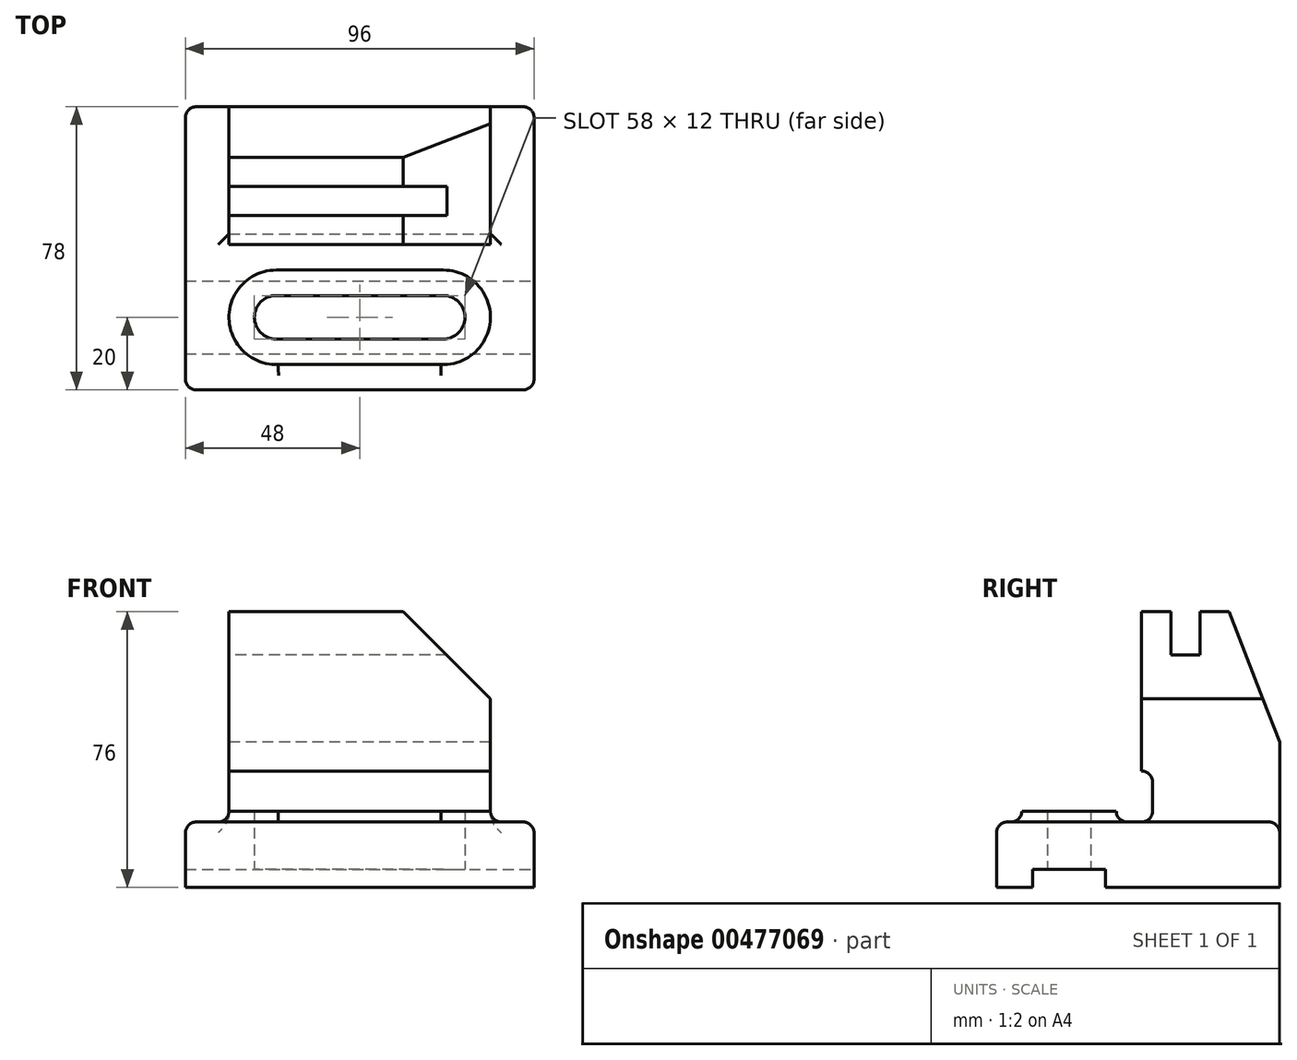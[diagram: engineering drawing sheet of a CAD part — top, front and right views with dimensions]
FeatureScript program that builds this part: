
annotation { "Feature Type Name" : "Feature", "Feature Type Description" : "" }
export const myFeature = defineFeature(function(context is Context, id is Id, definition is map)
    precondition{}
    {
        {
            var Q0;
            Q0=qCreatedBy(makeId("Top.planeOp"),FACE);
            var sketch = newSketch(context, id + "F0", { "sketchPlane" : qUnion([Q0])});
            skLineSegment(sketch, "E0.bottom", {"start": v(0, 0) * mm, "end": v(96, 0) * mm});
            skLineSegment(sketch, "E0.top", {"start": v(0, 78) * mm, "end": v(96, 78) * mm});
            skLineSegment(sketch, "E0.left", {"start": v(0, 0) * mm, "end": v(0, 78) * mm});
            skLineSegment(sketch, "E0.right", {"start": v(96, 0) * mm, "end": v(96, 78) * mm});
            skSolve(sketch);
        }
        {
            var Q0;
            Q0 = qSketchRegion(id + "F0", true);
            extrude(context, id + "F1", {"entities" : qUnion([Q0]), "depth" : 18 * mm});
        }
        {
            var Q0;
            Q0=makeQuery(id+"F1.opExtrude","CAP_FACE",FACE,{"disambiguationData":[OSD([sQuery(id+"F0.wireOp",EDGE,"E0.bottom"),sQuery(id+"F0.wireOp",EDGE,"E0.top"),sQuery(id+"F0.wireOp",EDGE,"E0.left"),sQuery(id+"F0.wireOp",EDGE,"E0.right")])],"isStart":false});
            var sketch = newSketch(context, id + "F2", { "sketchPlane" : qUnion([Q0])});
            skLineSegment(sketch, "E1.bottom", {"start": v(12, 78) * mm, "end": v(84, 78) * mm});
            skLineSegment(sketch, "E1.top", {"start": v(12, 40) * mm, "end": v(84, 40) * mm});
            skLineSegment(sketch, "E1.left", {"start": v(12, 78) * mm, "end": v(12, 40) * mm});
            skLineSegment(sketch, "E1.right", {"start": v(84, 78) * mm, "end": v(84, 40) * mm});
            skSolve(sketch);
        }
        {
            var Q0;
            Q0 = qSketchRegion(id + "F2", true);
            extrude(context, id + "F3", {"entities" : qUnion([Q0]), "operationType" : NewBodyOperationType.ADD, "depth" : 58 * mm});
        }
        {
            var Q0;
            Q0=makeQuery(id+"F1.opExtrude","SWEPT_FACE",FACE,{"disambiguationData":[OSD([sQuery(id+"F0.wireOp",EDGE,"E0.right")])]});
            var sketch = newSketch(context, id + "F4", { "sketchPlane" : qUnion([Q0])});
            skLineSegment(sketch, "E2.bottom", {"start": v(10, 0) * mm, "end": v(30, 0) * mm});
            skLineSegment(sketch, "E2.top", {"start": v(10, 5) * mm, "end": v(30, 5) * mm});
            skLineSegment(sketch, "E2.left", {"start": v(10, 0) * mm, "end": v(10, 5) * mm});
            skLineSegment(sketch, "E2.right", {"start": v(30, 0) * mm, "end": v(30, 5) * mm});
            skSolve(sketch);
        }
        {
            var Q0;
            Q0 = qSketchRegion(id + "F4", true);
            extrude(context, id + "F5", {"entities" : qUnion([Q0]), "operationType" : NewBodyOperationType.REMOVE, "endBound" : BoundingType.THROUGH_ALL, "oppositeDirection" : true, "depth" : 25 * mm});
        }
        {
            var Q0;
            Q0=makeQuery(id+"F3.opExtrude","SWEPT_FACE",FACE,{"disambiguationData":[OSD([sQuery(id+"F2.wireOp",EDGE,"E1.top")])]});
            var sketch = newSketch(context, id + "F6", { "sketchPlane" : qUnion([Q0])});
            skLineSegment(sketch, "E3.bottom", {"start": v(84, 76) * mm, "end": v(60, 76) * mm});
            skLineSegment(sketch, "E3.top", {"start": v(84, 52) * mm, "end": v(60, 52) * mm});
            skLineSegment(sketch, "E3.left", {"start": v(84, 76) * mm, "end": v(84, 52) * mm});
            skLineSegment(sketch, "E3.right", {"start": v(60, 76) * mm, "end": v(60, 52) * mm});
            skLineSegment(sketch, "E4", {"start": v(60, 76) * mm, "end": v(84, 52) * mm});
            skSolve(sketch);
        }
        {
            var Q0;
            Q0=makeQuery(id+"F6.imprint","IMPRINT",FACE,{"disambiguationData":[TD([[makeQuery(id+"F6.imprint","IMPRINT",EDGE,{"derivedFrom":sQuery(id+"F6.wireOp",EDGE,"E3.bottom")}),-1.0]])]});
            extrude(context, id + "F7", {"entities" : qUnion([Q0]), "operationType" : NewBodyOperationType.REMOVE, "endBound" : BoundingType.THROUGH_ALL, "oppositeDirection" : true, "depth" : 25 * mm});
        }
        {
            var Q0;
            Q0=makeQuery(id+"F3.opExtrude","SWEPT_FACE",FACE,{"disambiguationData":[OSD([sQuery(id+"F2.wireOp",EDGE,"E1.left")])]});
            var sketch = newSketch(context, id + "F8", { "sketchPlane" : qUnion([Q0])});
            skLineSegment(sketch, "E5.bottom", {"start": v(-40, 76) * mm, "end": v(-48, 76) * mm});
            skLineSegment(sketch, "E5.top", {"start": v(-40, 64) * mm, "end": v(-48, 64) * mm});
            skLineSegment(sketch, "E5.left", {"start": v(-40, 76) * mm, "end": v(-40, 64) * mm});
            skLineSegment(sketch, "E5.right", {"start": v(-48, 76) * mm, "end": v(-48, 64) * mm});
            skLineSegment(sketch, "E6.bottom", {"start": v(-48, 76) * mm, "end": v(-56, 76) * mm});
            skLineSegment(sketch, "E6.top", {"start": v(-48, 64) * mm, "end": v(-56, 64) * mm});
            skLineSegment(sketch, "E6.right", {"start": v(-56, 76) * mm, "end": v(-56, 64) * mm});
            skLineSegment(sketch, "E7", {"start": v(-56, 64) * mm, "end": v(-64, 64) * mm});
            skLineSegment(sketch, "E8", {"start": v(-64, 64) * mm, "end": v(-64, 76) * mm});
            skLineSegment(sketch, "E9.bottom", {"start": v(-78, 18) * mm, "end": v(-40, 18) * mm});
            skLineSegment(sketch, "E9.top", {"start": v(-78, 40) * mm, "end": v(-40, 40) * mm});
            skLineSegment(sketch, "E9.left", {"start": v(-78, 18) * mm, "end": v(-78, 40) * mm});
            skLineSegment(sketch, "E9.right", {"start": v(-40, 18) * mm, "end": v(-40, 40) * mm});
            skLineSegment(sketch, "E10", {"start": v(-78, 40) * mm, "end": v(-64, 76) * mm});
            skSolve(sketch);
        }
        {
            var Q0;
            Q0=makeQuery(id+"F8.imprint","IMPRINT",FACE,{"disambiguationData":[TD([[makeQuery(id+"F8.imprint","IMPRINT",EDGE,{"derivedFrom":sQuery(id+"F8.wireOp",EDGE,"E6.bottom")}),-1.0]])]});
            extrude(context, id + "F9", {"entities" : qUnion([Q0]), "operationType" : NewBodyOperationType.REMOVE, "endBound" : BoundingType.THROUGH_ALL, "oppositeDirection" : true, "depth" : 25 * mm});
        }
        {
            var Q0;
            {var subQ0=sQuery(id+"F8.wireOp",EDGE,"E10");Q0=makeQuery(id+"F8.imprint","IMPRINT",FACE,{"disambiguationData":[TD([[makeQuery(id+"F8.imprint","IMPRINT",EDGE,{"derivedFrom":subQ0}),1.0]])]});}
            extrude(context, id + "F10", {"entities" : qUnion([Q0]), "operationType" : NewBodyOperationType.REMOVE, "endBound" : BoundingType.THROUGH_ALL, "oppositeDirection" : true, "depth" : 25 * mm});
        }
        {
            var Q0;
            {var subQ0=sQuery(id+"F0.wireOp",EDGE,"E0.right");var subQ1=sQuery(id+"F0.wireOp",EDGE,"E0.top");Q0=makeQuery(id+"F3.boolean.opBoolean","SPLIT",EDGE,{"disambiguationData":[TD([makeQuery(id+"F1.opExtrude","SWEPT_FACE",FACE,{"disambiguationData":[OSD([subQ0])]})])],"derivedFrom":makeQuery(id+"F1.opExtrude","CAP_EDGE",EDGE,{"disambiguationData":[OSD([subQ1])],"isStart":false})});}
            fillet(context, id + "F11", {"entities" : qUnion([Q0]), "radius" : 3 * mm, "tangentPropagation" : true, "allowEdgeOverflow" : false});
        }
        {
            var Q0;
            Q0=makeQuery(id+"F1.opExtrude","SWEPT_EDGE",EDGE,{"disambiguationData":[OSD([sQuery(id+"F0.wireOp",EDGE,"E0.top"),sQuery(id+"F0.wireOp",EDGE,"E0.right")])]});
            var Q1;
            Q1=makeQuery(id+"F1.opExtrude","SWEPT_EDGE",EDGE,{"disambiguationData":[OSD([sQuery(id+"F0.wireOp",EDGE,"E0.bottom"),sQuery(id+"F0.wireOp",EDGE,"E0.right")])]});
            var Q2;
            Q2=makeQuery(id+"F1.opExtrude","SWEPT_EDGE",EDGE,{"disambiguationData":[OSD([sQuery(id+"F0.wireOp",EDGE,"E0.bottom"),sQuery(id+"F0.wireOp",EDGE,"E0.left")])]});
            var Q3;
            Q3=makeQuery(id+"F1.opExtrude","SWEPT_EDGE",EDGE,{"disambiguationData":[OSD([sQuery(id+"F0.wireOp",EDGE,"E0.top"),sQuery(id+"F0.wireOp",EDGE,"E0.left")])]});
            var Q4;
            Q4=makeQuery(id+"F1.opExtrude","CAP_EDGE",EDGE,{"disambiguationData":[OSD([sQuery(id+"F0.wireOp",EDGE,"E0.left")])],"isStart":false});
            var Q5;
            {var subQ0=sQuery(id+"F0.wireOp",EDGE,"E0.left");var subQ1=sQuery(id+"F0.wireOp",EDGE,"E0.top");Q5=makeQuery(id+"F3.boolean.opBoolean","SPLIT",EDGE,{"disambiguationData":[TD([makeQuery(id+"F1.opExtrude","SWEPT_FACE",FACE,{"disambiguationData":[OSD([subQ0])]})])],"derivedFrom":makeQuery(id+"F1.opExtrude","CAP_EDGE",EDGE,{"disambiguationData":[OSD([subQ1])],"isStart":false})});}
            fillet(context, id + "F12", {"entities" : qUnion([Q0, Q1, Q2, Q3, Q4, Q5]), "radius" : 3 * mm, "tangentPropagation" : true, "allowEdgeOverflow" : false});
        }
        {
            var Q0;
            Q0=makeQuery(id+"F3.opExtrude","SWEPT_FACE",FACE,{"disambiguationData":[OSD([sQuery(id+"F2.wireOp",EDGE,"E1.right")])]});
            var sketch = newSketch(context, id + "F13", { "sketchPlane" : qUnion([Q0])});
            skLineSegment(sketch, "E11.bottom", {"start": v(40, 18) * mm, "end": v(43, 18) * mm});
            skLineSegment(sketch, "E11.top", {"start": v(40, 32) * mm, "end": v(43, 32) * mm});
            skLineSegment(sketch, "E11.left", {"start": v(40, 18) * mm, "end": v(40, 32) * mm});
            skLineSegment(sketch, "E11.right", {"start": v(43, 18) * mm, "end": v(43, 32) * mm});
            skSolve(sketch);
        }
        {
            var Q0;
            Q0=makeQuery(id+"F13.imprint","IMPRINT",FACE,{"disambiguationData":[TD([[makeQuery(id+"F13.imprint","IMPRINT",EDGE,{"derivedFrom":sQuery(id+"F13.wireOp",EDGE,"E11.bottom")}),-1.0]])]});
            extrude(context, id + "F14", {"entities" : qUnion([Q0]), "operationType" : NewBodyOperationType.REMOVE, "endBound" : BoundingType.THROUGH_ALL, "oppositeDirection" : true, "depth" : 25 * mm});
        }
        {
            var Q0;
            Q0=makeQuery(id+"F14.boolean.opBoolean","COPY",EDGE,{"derivedFrom":makeQuery(id+"F14.opExtrude","SWEPT_EDGE",EDGE,{"disambiguationData":[OSD([sQuery(id+"F13.wireOp",EDGE,"E11.top"),sQuery(id+"F13.wireOp",EDGE,"E11.right")])]})});
            var Q1;
            Q1=makeQuery(id+"F14.boolean.opBoolean","COPY",EDGE,{"derivedFrom":makeQuery(id+"F14.opExtrude","SWEPT_EDGE",EDGE,{"disambiguationData":[OSD([sQuery(id+"F2.wireOp",EDGE,"E1.right"),sQuery(id+"F13.wireOp",EDGE,"E11.bottom"),sQuery(id+"F13.wireOp",EDGE,"E11.right")])]})});
            var Q2;
            Q2=makeQuery(id+"F3.opExtrude","CAP_EDGE",EDGE,{"disambiguationData":[OSD([sQuery(id+"F2.wireOp",EDGE,"E1.right")])],"isStart":true});
            var Q3;
            Q3=makeQuery(id+"F3.opExtrude","CAP_EDGE",EDGE,{"disambiguationData":[OSD([sQuery(id+"F2.wireOp",EDGE,"E1.left")])],"isStart":true});
            fillet(context, id + "F15", {"entities" : qUnion([Q0, Q1, Q2, Q3]), "radius" : 3 * mm, "tangentPropagation" : true, "allowEdgeOverflow" : false});
        }
        {
            var Q0;
            Q0=makeQuery(id+"F1.opExtrude","CAP_EDGE",EDGE,{"disambiguationData":[OSD([sQuery(id+"F0.wireOp",EDGE,"E0.bottom")])],"isStart":false});
            fillet(context, id + "F16", {"entities" : qUnion([Q0]), "radius" : 3 * mm, "tangentPropagation" : true, "allowEdgeOverflow" : false});
        }
        {
            var Q0;
            Q0=makeQuery(id+"F14.boolean.opBoolean","MERGE",FACE,{"derivedFrom":[makeQuery(id+"F1.opExtrude","CAP_FACE",FACE,{"disambiguationData":[OSD([sQuery(id+"F0.wireOp",EDGE,"E0.bottom"),sQuery(id+"F0.wireOp",EDGE,"E0.top"),sQuery(id+"F0.wireOp",EDGE,"E0.left"),sQuery(id+"F0.wireOp",EDGE,"E0.right")])],"isStart":false}),makeQuery(id+"F14.opExtrude","SWEPT_FACE",FACE,{"disambiguationData":[OSD([sQuery(id+"F13.wireOp",EDGE,"E11.bottom")])]})]});
            var sketch = newSketch(context, id + "F17", { "sketchPlane" : qUnion([Q0])});
            skLineSegment(sketch, "E12", {"start": v(25, 20) * mm, "end": v(71, 20) * mm, "construction": true});
            skLineSegment(sketch, "E13", {"start": v(25, 33) * mm, "end": v(71, 33) * mm});
            skLineSegment(sketch, "E14", {"start": v(25, 7.01) * mm, "end": v(71, 7.01) * mm});
            skArc(sketch, "E15", {"start": v(25, 33) * mm, "mid": v(12, 19.71) * mm, "end": v(25.57, 7.01) * mm});
            skArc(sketch, "E16", {"start": v(70.43, 7.01) * mm, "mid": v(84, 19.71) * mm, "end": v(71, 33) * mm});
            skLineSegment(sketch, "E17", {"start": v(25, 26) * mm, "end": v(71, 26) * mm});
            skLineSegment(sketch, "E18", {"start": v(25, 14) * mm, "end": v(71, 14) * mm});
            skArc(sketch, "E19", {"start": v(25, 26) * mm, "mid": v(19, 20) * mm, "end": v(25, 14) * mm});
            skArc(sketch, "E20", {"start": v(71, 14) * mm, "mid": v(77, 20) * mm, "end": v(71, 26) * mm});
            skSolve(sketch);
        }
        {
            var Q0;
            Q0=makeQuery(id+"F17.imprint","IMPRINT",FACE,{"disambiguationData":[TD([[makeQuery(id+"F17.imprint","IMPRINT",EDGE,{"derivedFrom":sQuery(id+"F17.wireOp",EDGE,"E13")}),-1.0]])]});
            extrude(context, id + "F18", {"entities" : qUnion([Q0]), "operationType" : NewBodyOperationType.ADD, "depth" : 3 * mm});
        }
        {
            var Q0;
            Q0=makeQuery(id+"F18.boolean.opBoolean","SPLIT",FACE,{"disambiguationData":[TD([makeQuery(id+"F18.opExtrude","SWEPT_FACE",FACE,{"disambiguationData":[OSD([sQuery(id+"F17.wireOp",EDGE,"E17")])]})])],"derivedFrom":makeQuery(id+"F14.boolean.opBoolean","MERGE",FACE,{"derivedFrom":[makeQuery(id+"F1.opExtrude","CAP_FACE",FACE,{"disambiguationData":[OSD([sQuery(id+"F0.wireOp",EDGE,"E0.bottom"),sQuery(id+"F0.wireOp",EDGE,"E0.top"),sQuery(id+"F0.wireOp",EDGE,"E0.left"),sQuery(id+"F0.wireOp",EDGE,"E0.right")])],"isStart":false}),makeQuery(id+"F14.opExtrude","SWEPT_FACE",FACE,{"disambiguationData":[OSD([sQuery(id+"F13.wireOp",EDGE,"E11.bottom")])]})]})});
            extrude(context, id + "F19", {"entities" : qUnion([Q0]), "operationType" : NewBodyOperationType.REMOVE, "endBound" : BoundingType.THROUGH_ALL, "oppositeDirection" : true, "depth" : 25 * mm});
        }
        {
            var Q0;
            Q0=makeQuery(id+"F18.opExtrude","CAP_EDGE",EDGE,{"disambiguationData":[OSD([sQuery(id+"F17.wireOp",EDGE,"E14")])],"isStart":true});
            var Q1;
            Q1=makeQuery(id+"F18.opExtrude","CAP_EDGE",EDGE,{"disambiguationData":[OSD([sQuery(id+"F17.wireOp",EDGE,"E16")])],"isStart":true});
            var Q2;
            Q2=makeQuery(id+"F18.opExtrude","CAP_EDGE",EDGE,{"disambiguationData":[OSD([sQuery(id+"F17.wireOp",EDGE,"E15")])],"isStart":true});
            var Q3;
            {var subQ2=sQuery(id+"F0.wireOp",EDGE,"E0.top");var subQ3=sQuery(id+"F0.wireOp",EDGE,"E0.left");var subQ4=sQuery(id+"F0.wireOp",EDGE,"E0.right");var subQ5=sQuery(id+"F0.wireOp",EDGE,"E0.bottom");var subQ7=makeQuery(id+"F1.opExtrude","CAP_FACE",FACE,{"disambiguationData":[OSD([subQ5,subQ2,subQ3,subQ4])],"isStart":false});var subQ8=sQuery(id+"F13.wireOp",EDGE,"E11.bottom");Q3=makeQuery(id+"F18.boolean.opBoolean","SPLIT",FACE,{"disambiguationData":[TD([makeQuery(id+"F11.opFillet","BLEND_FACE",FACE,{"disambiguationData":[OSD([subQ2])]})])],"derivedFrom":makeQuery(id+"F14.boolean.opBoolean","MERGE",FACE,{"derivedFrom":[subQ7,makeQuery(id+"F14.opExtrude","SWEPT_FACE",FACE,{"disambiguationData":[OSD([subQ8])]})]})});}
            fillet(context, id + "F20", {"entities" : qUnion([Q0, Q1, Q2, Q3]), "radius" : 3 * mm, "tangentPropagation" : true, "allowEdgeOverflow" : false});
        }
    });
